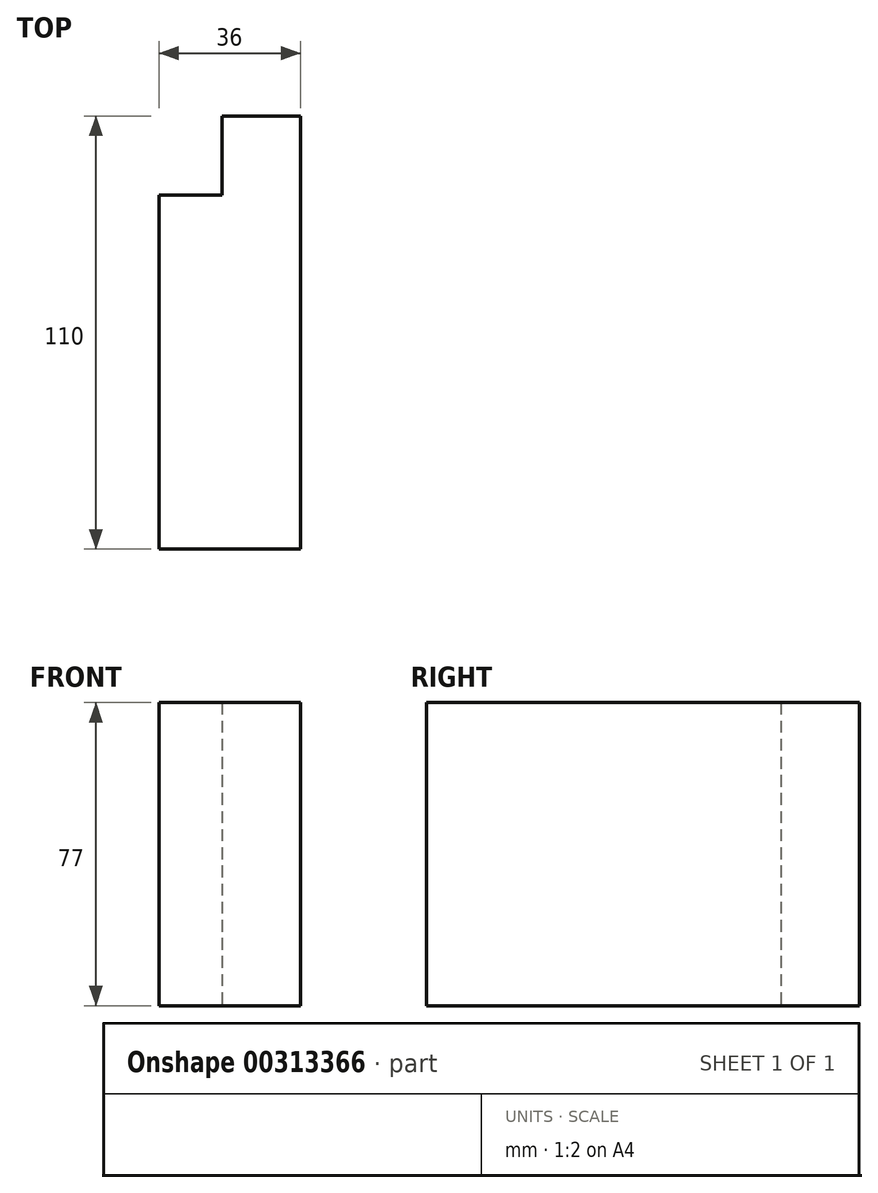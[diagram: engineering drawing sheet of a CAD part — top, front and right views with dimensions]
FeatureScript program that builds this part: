
annotation { "Feature Type Name" : "Feature", "Feature Type Description" : "" }
export const myFeature = defineFeature(function(context is Context, id is Id, definition is map)
    precondition{}
    {
        {
            var Q0;
            Q0=qCreatedBy(makeId("Right.planeOp"),FACE);
            var sketch = newSketch(context, id + "F0", { "sketchPlane" : qUnion([Q0])});
            skLineSegment(sketch, "E0.bottom", {"start": v(-55, 77) * mm, "end": v(55, 77) * mm});
            skLineSegment(sketch, "E0.top", {"start": v(-55, 0) * mm, "end": v(55, 0) * mm});
            skLineSegment(sketch, "E0.left", {"start": v(-55, 77) * mm, "end": v(-55, 0) * mm});
            skLineSegment(sketch, "E0.right", {"start": v(55, 77) * mm, "end": v(55, 0) * mm});
            skPoint(sketch, "E1", {"position": v(0, 0) * mm});
            skLineSegment(sketch, "E2", {"start": v(35, 77) * mm, "end": v(35, 0) * mm});
            skSolve(sketch);
        }
        {
            var Q0;
            {var subQ0=sQuery(id+"F0.wireOp",EDGE,"E0.right");Q0=makeQuery(id+"F0.imprint","IMPRINT",FACE,{"disambiguationData":[TD([[makeQuery(id+"F0.imprint","IMPRINT",EDGE,{"derivedFrom":subQ0}),-1.0]])]});}
            extrude(context, id + "F1", {"entities" : qUnion([Q0]), "oppositeDirection" : true, "depth" : 20 * mm});
        }
        {
            var Q0;
            {var subQ0=sQuery(id+"F0.wireOp",EDGE,"E0.left");Q0=makeQuery(id+"F0.imprint","IMPRINT",FACE,{"disambiguationData":[TD([[makeQuery(id+"F0.imprint","IMPRINT",EDGE,{"derivedFrom":subQ0}),1.0]])]});}
            extrude(context, id + "F2", {"entities" : qUnion([Q0]), "operationType" : NewBodyOperationType.ADD, "oppositeDirection" : true, "depth" : 36 * mm});
        }
    });
